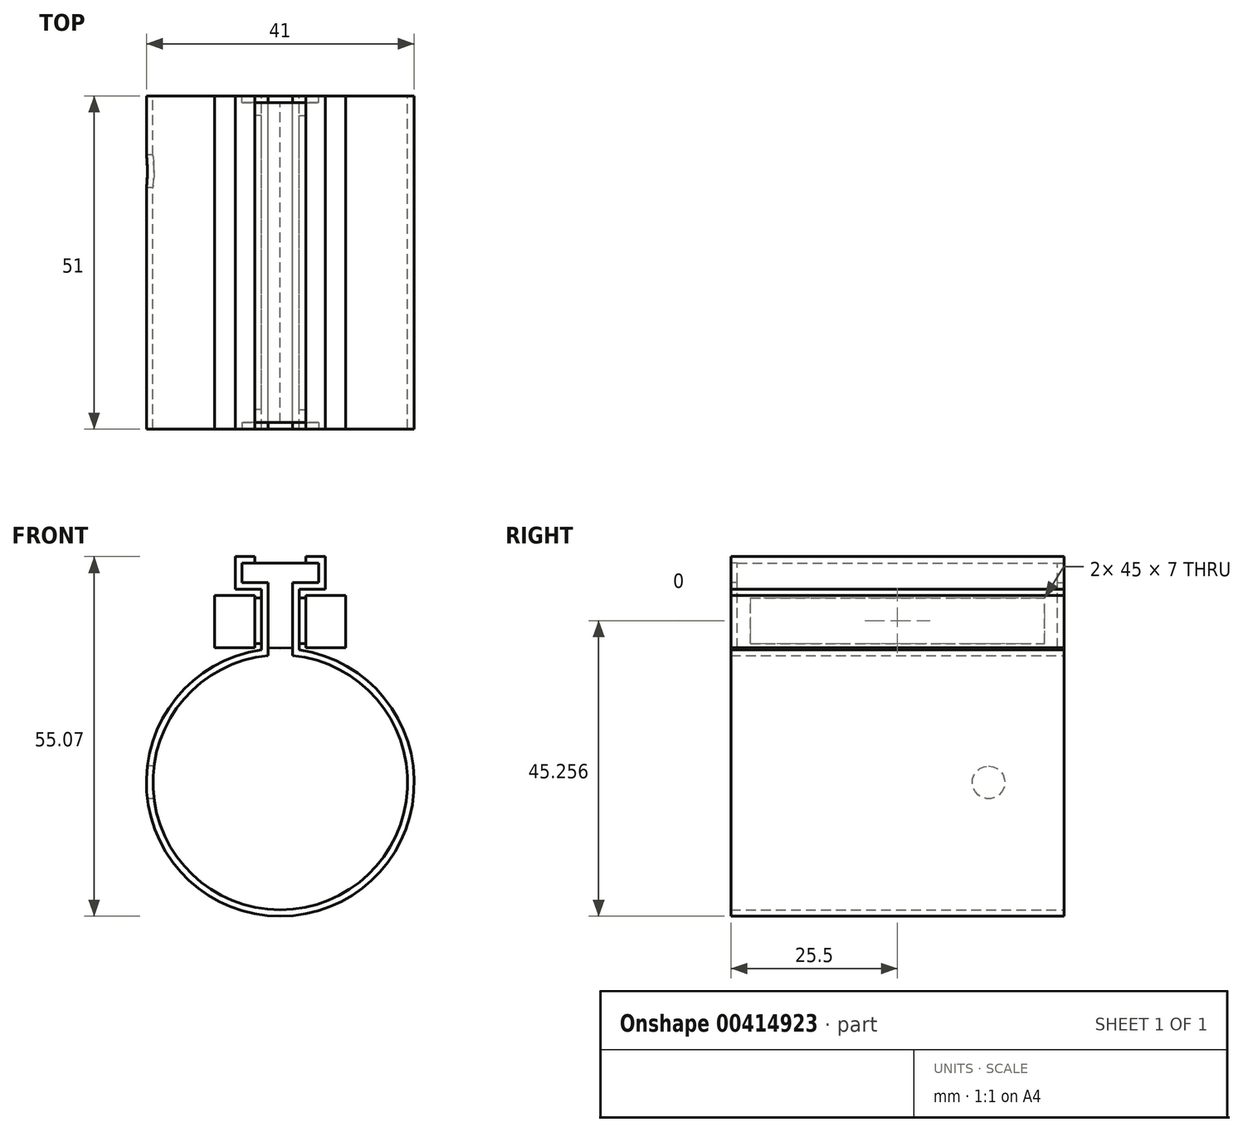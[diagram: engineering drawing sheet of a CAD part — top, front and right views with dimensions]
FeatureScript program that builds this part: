
annotation { "Feature Type Name" : "Feature", "Feature Type Description" : "" }
export const myFeature = defineFeature(function(context is Context, id is Id, definition is map)
    precondition{}
    {
        {
            var Q0;
            Q0=qCreatedBy(makeId("Front.planeOp"),FACE);
            var sketch = newSketch(context, id + "F0", { "sketchPlane" : qUnion([Q0])});
            skArc(sketch, "E0", {"start": v(0, -19.5) * mm, "mid": v(19.48, -0.94) * mm, "end": v(1.88, 19.4) * mm});
            skLineSegment(sketch, "E1", {"start": v(0, 19.5) * mm, "end": v(0, 19.5) * mm});
            skLineSegment(sketch, "E2", {"start": v(1.88, 30.57) * mm, "end": v(5.88, 30.57) * mm});
            skLineSegment(sketch, "E3", {"start": v(5.88, 30.57) * mm, "end": v(5.88, 33.57) * mm});
            skLineSegment(sketch, "E4", {"start": v(5.88, 33.57) * mm, "end": v(3.88, 33.57) * mm});
            skLineSegment(sketch, "E5.0", {"start": v(6.88, 34.57) * mm, "end": v(3.88, 34.57) * mm});
            skLineSegment(sketch, "E5.1", {"start": v(6.88, 29.57) * mm, "end": v(6.88, 34.57) * mm});
            skLineSegment(sketch, "E5.2", {"start": v(2.88, 29.57) * mm, "end": v(6.88, 29.57) * mm});
            skLineSegment(sketch, "E5.3", {"start": v(2.88, 20.3) * mm, "end": v(2.88, 29.57) * mm});
            skLineSegment(sketch, "E6", {"start": v(3.88, 34.57) * mm, "end": v(3.88, 33.57) * mm});
            skLineSegment(sketch, "E7.trimOffspring", {"start": v(1.88, 20.58) * mm, "end": v(1.88, 30.57) * mm});
            skArc(sketch, "E8", {"start": v(0, -20.5) * mm, "mid": v(20.45, -1.44) * mm, "end": v(2.88, 20.3) * mm});
            skLineSegment(sketch, "E9", {"start": v(0, -19.5) * mm, "end": v(0, -20.5) * mm});
            skLineSegment(sketch, "E10", {"start": v(1.88, 20.58) * mm, "end": v(1.88, 19.4) * mm});
            skLineSegment(sketch, "E11", {"start": v(2.88, 21.26) * mm, "end": v(3.88, 21.26) * mm});
            skLineSegment(sketch, "E12", {"start": v(3.88, 21.26) * mm, "end": v(3.88, 28.26) * mm});
            skLineSegment(sketch, "E13", {"start": v(3.88, 28.26) * mm, "end": v(2.88, 28.26) * mm});
            skLineSegment(sketch, "E14", {"start": v(3.88, 28.26) * mm, "end": v(3.88, 28.64) * mm});
            skLineSegment(sketch, "E15", {"start": v(3.88, 28.64) * mm, "end": v(10.04, 28.64) * mm});
            skLineSegment(sketch, "E16", {"start": v(10.04, 28.64) * mm, "end": v(10.04, 20.64) * mm});
            skLineSegment(sketch, "E17", {"start": v(3.88, 21.26) * mm, "end": v(3.88, 20.64) * mm});
            skLineSegment(sketch, "E18", {"start": v(3.88, 20.64) * mm, "end": v(10.04, 20.64) * mm});
            skLineSegment(sketch, "E19", {"start": v(0, 20.56) * mm, "end": v(0, 33.57) * mm});
            skLineSegment(sketch, "E20", {"start": v(0, 33.57) * mm, "end": v(3.88, 33.57) * mm});
            skLineSegment(sketch, "E21", {"start": v(3.88, 33.57) * mm, "end": v(3.88, 33.57) * mm});
            skLineSegment(sketch, "E22", {"start": v(5.88, 33.57) * mm, "end": v(5.88, 30.57) * mm});
            skLineSegment(sketch, "E23", {"start": v(1.88, 30.57) * mm, "end": v(1.88, 20.58) * mm});
            skLineSegment(sketch, "E24", {"start": v(0, 20.56) * mm, "end": v(1.88, 20.58) * mm});
            skSolve(sketch);
        }
        {
            var Q0;
            Q0 = qSketchRegion(id + "F0", true);
            extrude(context, id + "F1", {"entities" : qUnion([Q0]), "endBound" : BoundingType.SYMMETRIC, "depth" : 51 * mm});
        }
        {
            var Q0;
            Q0=makeQuery(id+"F1.opExtrude","CAP_FACE",FACE,{"disambiguationData":[OSD([sQuery(id+"F0.wireOp",EDGE,"E0"),sQuery(id+"F0.wireOp",EDGE,"E2"),sQuery(id+"F0.wireOp",EDGE,"E3"),sQuery(id+"F0.wireOp",EDGE,"E4"),sQuery(id+"F0.wireOp",EDGE,"E5.0"),sQuery(id+"F0.wireOp",EDGE,"E5.1"),sQuery(id+"F0.wireOp",EDGE,"E5.2"),sQuery(id+"F0.wireOp",EDGE,"E5.3"),sQuery(id+"F0.wireOp",EDGE,"E6"),sQuery(id+"F0.wireOp",EDGE,"E7.trimOffspring"),sQuery(id+"F0.wireOp",EDGE,"E8"),sQuery(id+"F0.wireOp",EDGE,"E9"),sQuery(id+"F0.wireOp",EDGE,"E10"),sQuery(id+"F0.wireOp",EDGE,"E11"),sQuery(id+"F0.wireOp",EDGE,"E13"),sQuery(id+"F0.wireOp",EDGE,"E14"),sQuery(id+"F0.wireOp",EDGE,"E15"),sQuery(id+"F0.wireOp",EDGE,"E16"),sQuery(id+"F0.wireOp",EDGE,"E17"),sQuery(id+"F0.wireOp",EDGE,"E18")])],"isStart":false});
            var sketch = newSketch(context, id + "F2", { "sketchPlane" : qUnion([Q0])});
            skArc(sketch, "E25.0", {"start": v(0, -19.5) * mm, "mid": v(19.48, -0.94) * mm, "end": v(1.88, 19.4) * mm});
            skPoint(sketch, "E25.1", {"position": v(0, 19.5) * mm});
            skLineSegment(sketch, "E25.2", {"start": v(1.88, 30.57) * mm, "end": v(5.88, 30.57) * mm});
            skLineSegment(sketch, "E25.3", {"start": v(5.88, 30.57) * mm, "end": v(5.88, 33.57) * mm});
            skLineSegment(sketch, "E25.4", {"start": v(5.88, 33.57) * mm, "end": v(3.88, 33.57) * mm});
            skLineSegment(sketch, "E25.5", {"start": v(6.88, 34.57) * mm, "end": v(3.88, 34.57) * mm});
            skLineSegment(sketch, "E25.6", {"start": v(6.88, 29.57) * mm, "end": v(6.88, 34.57) * mm});
            skLineSegment(sketch, "E25.7", {"start": v(2.88, 29.57) * mm, "end": v(6.88, 29.57) * mm});
            skLineSegment(sketch, "E25.8", {"start": v(2.88, 20.3) * mm, "end": v(2.88, 29.57) * mm});
            skLineSegment(sketch, "E25.9", {"start": v(3.88, 34.57) * mm, "end": v(3.88, 33.57) * mm});
            skLineSegment(sketch, "E25.10", {"start": v(1.88, 20.58) * mm, "end": v(1.88, 30.57) * mm});
            skArc(sketch, "E25.11", {"start": v(0, -20.5) * mm, "mid": v(20.45, -1.44) * mm, "end": v(2.88, 20.3) * mm});
            skLineSegment(sketch, "E25.12", {"start": v(0, -19.5) * mm, "end": v(0, -20.5) * mm});
            skLineSegment(sketch, "E25.13", {"start": v(1.88, 20.58) * mm, "end": v(1.88, 19.4) * mm});
            skLineSegment(sketch, "E25.14", {"start": v(2.88, 21.26) * mm, "end": v(3.88, 21.26) * mm});
            skLineSegment(sketch, "E25.15", {"start": v(3.88, 21.26) * mm, "end": v(3.88, 28.26) * mm});
            skLineSegment(sketch, "E25.16", {"start": v(3.88, 28.26) * mm, "end": v(2.88, 28.26) * mm});
            skLineSegment(sketch, "E25.17", {"start": v(3.88, 28.26) * mm, "end": v(3.88, 28.64) * mm});
            skLineSegment(sketch, "E25.18", {"start": v(3.88, 28.64) * mm, "end": v(10.04, 28.64) * mm});
            skLineSegment(sketch, "E25.19", {"start": v(10.04, 28.64) * mm, "end": v(10.04, 20.64) * mm});
            skLineSegment(sketch, "E25.20", {"start": v(3.88, 21.26) * mm, "end": v(3.88, 20.64) * mm});
            skLineSegment(sketch, "E25.21", {"start": v(3.88, 20.64) * mm, "end": v(10.04, 20.64) * mm});
            skLineSegment(sketch, "E25.22", {"start": v(10.04, 28.64) * mm, "end": v(10.04, 20.64) * mm});
            skSolve(sketch);
        }
        {
            var Q0;
            {var subQ0=sQuery(id+"F2.wireOp",EDGE,"E25.14");Q0=makeQuery(id+"F2.imprint","IMPRINT",FACE,{"disambiguationData":[TD([[makeQuery(id+"F2.imprint","IMPRINT",EDGE,{"derivedFrom":subQ0}),1.0]])]});}
            extrude(context, id + "F3", {"entities" : qUnion([Q0]), "operationType" : NewBodyOperationType.REMOVE, "oppositeDirection" : true, "depth" : 3 * mm});
        }
        {
            var Q0;
            Q0=makeQuery(id+"F1.opExtrude","CAP_FACE",FACE,{"disambiguationData":[OSD([sQuery(id+"F0.wireOp",EDGE,"E0"),sQuery(id+"F0.wireOp",EDGE,"E2"),sQuery(id+"F0.wireOp",EDGE,"E3"),sQuery(id+"F0.wireOp",EDGE,"E4"),sQuery(id+"F0.wireOp",EDGE,"E5.0"),sQuery(id+"F0.wireOp",EDGE,"E5.1"),sQuery(id+"F0.wireOp",EDGE,"E5.2"),sQuery(id+"F0.wireOp",EDGE,"E5.3"),sQuery(id+"F0.wireOp",EDGE,"E6"),sQuery(id+"F0.wireOp",EDGE,"E7.trimOffspring"),sQuery(id+"F0.wireOp",EDGE,"E8"),sQuery(id+"F0.wireOp",EDGE,"E9"),sQuery(id+"F0.wireOp",EDGE,"E10"),sQuery(id+"F0.wireOp",EDGE,"E11"),sQuery(id+"F0.wireOp",EDGE,"E13"),sQuery(id+"F0.wireOp",EDGE,"E14"),sQuery(id+"F0.wireOp",EDGE,"E15"),sQuery(id+"F0.wireOp",EDGE,"E16"),sQuery(id+"F0.wireOp",EDGE,"E17"),sQuery(id+"F0.wireOp",EDGE,"E18")])],"isStart":true});
            var sketch = newSketch(context, id + "F4", { "sketchPlane" : qUnion([Q0])});
            skArc(sketch, "E26.0", {"start": v(0, -19.5) * mm, "mid": v(-19.48, -0.94) * mm, "end": v(-1.88, 19.4) * mm});
            skPoint(sketch, "E26.1", {"position": v(0, 19.5) * mm});
            skLineSegment(sketch, "E26.2", {"start": v(-1.88, 30.57) * mm, "end": v(-5.88, 30.57) * mm});
            skLineSegment(sketch, "E26.3", {"start": v(-5.88, 30.57) * mm, "end": v(-5.88, 33.57) * mm});
            skLineSegment(sketch, "E26.4", {"start": v(-5.88, 33.57) * mm, "end": v(-3.88, 33.57) * mm});
            skLineSegment(sketch, "E26.5", {"start": v(-6.88, 34.57) * mm, "end": v(-3.88, 34.57) * mm});
            skLineSegment(sketch, "E26.6", {"start": v(-6.88, 29.57) * mm, "end": v(-6.88, 34.57) * mm});
            skLineSegment(sketch, "E26.7", {"start": v(-2.88, 29.57) * mm, "end": v(-6.88, 29.57) * mm});
            skLineSegment(sketch, "E26.8", {"start": v(-2.88, 20.3) * mm, "end": v(-2.88, 29.57) * mm});
            skLineSegment(sketch, "E26.9", {"start": v(-3.88, 34.57) * mm, "end": v(-3.88, 33.57) * mm});
            skLineSegment(sketch, "E26.10", {"start": v(-1.88, 20.58) * mm, "end": v(-1.88, 30.57) * mm});
            skArc(sketch, "E26.11", {"start": v(0, -20.5) * mm, "mid": v(-20.45, -1.44) * mm, "end": v(-2.88, 20.3) * mm});
            skLineSegment(sketch, "E26.12", {"start": v(0, -19.5) * mm, "end": v(0, -20.5) * mm});
            skLineSegment(sketch, "E26.13", {"start": v(-1.88, 20.58) * mm, "end": v(-1.88, 19.4) * mm});
            skLineSegment(sketch, "E26.14", {"start": v(-2.88, 21.26) * mm, "end": v(-3.88, 21.26) * mm});
            skLineSegment(sketch, "E26.15", {"start": v(-3.88, 21.26) * mm, "end": v(-3.88, 28.26) * mm});
            skLineSegment(sketch, "E26.16", {"start": v(-3.88, 28.26) * mm, "end": v(-2.88, 28.26) * mm});
            skLineSegment(sketch, "E26.17", {"start": v(-3.88, 28.26) * mm, "end": v(-3.88, 28.64) * mm});
            skLineSegment(sketch, "E26.18", {"start": v(-3.88, 28.64) * mm, "end": v(-10.04, 28.64) * mm});
            skLineSegment(sketch, "E26.19", {"start": v(-10.04, 28.64) * mm, "end": v(-10.04, 20.64) * mm});
            skLineSegment(sketch, "E26.20", {"start": v(-3.88, 21.26) * mm, "end": v(-3.88, 20.64) * mm});
            skLineSegment(sketch, "E26.21", {"start": v(-3.88, 20.64) * mm, "end": v(-10.04, 20.64) * mm});
            skLineSegment(sketch, "E26.22.0", {"start": v(-10.04, 20.64) * mm, "end": v(-10.04, 28.64) * mm});
            skLineSegment(sketch, "E26.22.2", {"start": v(-10.04, 28.64) * mm, "end": v(-10.04, 20.64) * mm});
            skSolve(sketch);
        }
        {
            var Q0;
            {var subQ0=sQuery(id+"F4.wireOp",EDGE,"E26.14");Q0=makeQuery(id+"F4.imprint","IMPRINT",FACE,{"disambiguationData":[TD([[makeQuery(id+"F4.imprint","IMPRINT",EDGE,{"derivedFrom":subQ0}),-1.0]])]});}
            extrude(context, id + "F5", {"entities" : qUnion([Q0]), "operationType" : NewBodyOperationType.REMOVE, "oppositeDirection" : true, "depth" : 3 * mm});
        }
        {
            var Q0;
            {var subQ0=sQuery(id+"F0.wireOp",EDGE,"E10");var subQ1=sQuery(id+"F0.wireOp",EDGE,"E9");var subQ2=sQuery(id+"F0.wireOp",EDGE,"E8");var subQ3=sQuery(id+"F0.wireOp",EDGE,"E19");var subQ4=sQuery(id+"F0.wireOp",EDGE,"E5.3");var subQ5=sQuery(id+"F0.wireOp",EDGE,"E5.2");var subQ6=sQuery(id+"F0.wireOp",EDGE,"E13");var subQ7=sQuery(id+"F0.wireOp",EDGE,"E11");var subQ8=sQuery(id+"F0.wireOp",EDGE,"E0");var subQ9=sQuery(id+"F0.wireOp",EDGE,"E5.0");var subQ10=sQuery(id+"F0.wireOp",EDGE,"E5.1");var subQ11=sQuery(id+"F0.wireOp",EDGE,"E20");var subQ12=sQuery(id+"F0.wireOp",EDGE,"E21");var subQ13=sQuery(id+"F0.wireOp",EDGE,"E24");var subQ14=makeQuery(id+"F3.boolean.opBoolean","SPLIT",FACE,{"disambiguationData":[TD([makeQuery(id+"F1.opExtrude","SWEPT_FACE",FACE,{"disambiguationData":[OSD([subQ8])]})])],"derivedFrom":makeQuery(id+"F1.opExtrude","CAP_FACE",FACE,{"disambiguationData":[OSD([subQ8,subQ9,subQ10,subQ5,subQ4,subQ2,subQ1,subQ0,subQ7,subQ6,sQuery(id+"F0.wireOp",EDGE,"E14"),sQuery(id+"F0.wireOp",EDGE,"E15"),sQuery(id+"F0.wireOp",EDGE,"E16"),sQuery(id+"F0.wireOp",EDGE,"E17"),sQuery(id+"F0.wireOp",EDGE,"E18"),subQ3,subQ11,subQ12,subQ13])],"isStart":false})});Q0=makeQuery(id+"F10.boolean.opBoolean","MERGE",FACE,{"derivedFrom":[subQ14,makeQuery(id+"F10.opPattern","COPY",FACE,{"derivedFrom":subQ14,"instanceName":"1"})]});}
            var sketch = newSketch(context, id + "F6", { "sketchPlane" : qUnion([Q0])});
            skArc(sketch, "E27.0", {"start": v(0, -19.5) * mm, "mid": v(19.48, -0.94) * mm, "end": v(1.88, 19.4) * mm});
            skPoint(sketch, "E27.1", {"position": v(0, 19.5) * mm});
            skLineSegment(sketch, "E27.2", {"start": v(1.88, 30.57) * mm, "end": v(5.88, 30.57) * mm});
            skLineSegment(sketch, "E27.3", {"start": v(5.88, 30.57) * mm, "end": v(5.88, 33.57) * mm});
            skLineSegment(sketch, "E27.4", {"start": v(5.88, 33.57) * mm, "end": v(3.88, 33.57) * mm});
            skLineSegment(sketch, "E27.5", {"start": v(6.88, 34.57) * mm, "end": v(3.88, 34.57) * mm});
            skLineSegment(sketch, "E27.6", {"start": v(6.88, 29.57) * mm, "end": v(6.88, 34.57) * mm});
            skLineSegment(sketch, "E27.7", {"start": v(2.88, 29.57) * mm, "end": v(6.88, 29.57) * mm});
            skLineSegment(sketch, "E27.8", {"start": v(2.88, 20.3) * mm, "end": v(2.88, 29.57) * mm});
            skLineSegment(sketch, "E27.9", {"start": v(3.88, 34.57) * mm, "end": v(3.88, 33.57) * mm});
            skLineSegment(sketch, "E27.10", {"start": v(1.88, 20.58) * mm, "end": v(1.88, 30.57) * mm});
            skArc(sketch, "E27.11", {"start": v(0, -20.5) * mm, "mid": v(20.45, -1.44) * mm, "end": v(2.88, 20.3) * mm});
            skLineSegment(sketch, "E27.12", {"start": v(0, -19.5) * mm, "end": v(0, -20.5) * mm});
            skLineSegment(sketch, "E27.13", {"start": v(1.88, 20.58) * mm, "end": v(1.88, 19.4) * mm});
            skLineSegment(sketch, "E27.14", {"start": v(2.88, 21.26) * mm, "end": v(3.88, 21.26) * mm});
            skLineSegment(sketch, "E27.15", {"start": v(3.88, 21.26) * mm, "end": v(3.88, 28.26) * mm});
            skLineSegment(sketch, "E27.16", {"start": v(3.88, 28.26) * mm, "end": v(2.88, 28.26) * mm});
            skLineSegment(sketch, "E27.17", {"start": v(3.88, 28.26) * mm, "end": v(3.88, 28.64) * mm});
            skLineSegment(sketch, "E27.18", {"start": v(3.88, 28.64) * mm, "end": v(10.04, 28.64) * mm});
            skLineSegment(sketch, "E27.19", {"start": v(10.04, 28.64) * mm, "end": v(10.04, 20.64) * mm});
            skLineSegment(sketch, "E27.20", {"start": v(3.88, 21.26) * mm, "end": v(3.88, 20.64) * mm});
            skLineSegment(sketch, "E27.21", {"start": v(3.88, 20.64) * mm, "end": v(10.04, 20.64) * mm});
            skLineSegment(sketch, "E27.22", {"start": v(0, 20.56) * mm, "end": v(0, 33.57) * mm});
            skLineSegment(sketch, "E27.23", {"start": v(0, 33.57) * mm, "end": v(3.88, 33.57) * mm});
            skLineSegment(sketch, "E27.24", {"start": v(3.88, 33.57) * mm, "end": v(3.88, 33.57) * mm});
            skLineSegment(sketch, "E27.25", {"start": v(5.88, 33.57) * mm, "end": v(5.88, 30.57) * mm});
            skLineSegment(sketch, "E27.26", {"start": v(1.88, 30.57) * mm, "end": v(1.88, 20.58) * mm});
            skLineSegment(sketch, "E27.27", {"start": v(0, 20.56) * mm, "end": v(1.88, 20.58) * mm});
            skLineSegment(sketch, "E27.28.0", {"start": v(6.88, 29.57) * mm, "end": v(6.88, 34.57) * mm});
            skLineSegment(sketch, "E27.28.2", {"start": v(6.88, 34.57) * mm, "end": v(6.88, 29.57) * mm});
            skSolve(sketch);
        }
        {
            var Q0;
            Q0=makeQuery(id+"F6.imprint","IMPRINT",FACE,{"disambiguationData":[TD([[makeQuery(id+"F6.imprint","IMPRINT",EDGE,{"derivedFrom":sQuery(id+"F6.wireOp",EDGE,"E27.2")}),1.0]])]});
            extrude(context, id + "F7", {"entities" : qUnion([Q0]), "operationType" : NewBodyOperationType.REMOVE, "oppositeDirection" : true, "depth" : 1 * mm});
        }
        {
            var Q0;
            {var subQ0=sQuery(id+"F0.wireOp",EDGE,"E10");var subQ1=sQuery(id+"F0.wireOp",EDGE,"E9");var subQ2=sQuery(id+"F0.wireOp",EDGE,"E8");var subQ3=sQuery(id+"F0.wireOp",EDGE,"E19");var subQ4=sQuery(id+"F0.wireOp",EDGE,"E5.3");var subQ5=sQuery(id+"F0.wireOp",EDGE,"E5.2");var subQ6=sQuery(id+"F0.wireOp",EDGE,"E13");var subQ7=sQuery(id+"F0.wireOp",EDGE,"E11");var subQ8=sQuery(id+"F0.wireOp",EDGE,"E0");var subQ9=sQuery(id+"F0.wireOp",EDGE,"E5.0");var subQ10=sQuery(id+"F0.wireOp",EDGE,"E5.1");var subQ11=sQuery(id+"F0.wireOp",EDGE,"E20");var subQ12=sQuery(id+"F0.wireOp",EDGE,"E21");var subQ13=sQuery(id+"F0.wireOp",EDGE,"E24");var subQ14=makeQuery(id+"F5.boolean.opBoolean","SPLIT",FACE,{"disambiguationData":[TD([makeQuery(id+"F1.opExtrude","SWEPT_FACE",FACE,{"disambiguationData":[OSD([subQ8])]})])],"derivedFrom":makeQuery(id+"F1.opExtrude","CAP_FACE",FACE,{"disambiguationData":[OSD([subQ8,subQ9,subQ10,subQ5,subQ4,subQ2,subQ1,subQ0,subQ7,subQ6,sQuery(id+"F0.wireOp",EDGE,"E14"),sQuery(id+"F0.wireOp",EDGE,"E15"),sQuery(id+"F0.wireOp",EDGE,"E16"),sQuery(id+"F0.wireOp",EDGE,"E17"),sQuery(id+"F0.wireOp",EDGE,"E18"),subQ3,subQ11,subQ12,subQ13])],"isStart":true})});Q0=makeQuery(id+"F10.boolean.opBoolean","MERGE",FACE,{"derivedFrom":[subQ14,makeQuery(id+"F10.opPattern","COPY",FACE,{"derivedFrom":subQ14,"instanceName":"1"})]});}
            var sketch = newSketch(context, id + "F8", { "sketchPlane" : qUnion([Q0])});
            skArc(sketch, "E28.0", {"start": v(0, -19.5) * mm, "mid": v(-19.48, -0.94) * mm, "end": v(-1.88, 19.4) * mm});
            skPoint(sketch, "E28.1", {"position": v(0, 19.5) * mm});
            skLineSegment(sketch, "E28.2", {"start": v(-1.88, 30.57) * mm, "end": v(-5.88, 30.57) * mm});
            skLineSegment(sketch, "E28.3", {"start": v(-5.88, 30.57) * mm, "end": v(-5.88, 33.57) * mm});
            skLineSegment(sketch, "E28.4", {"start": v(-5.88, 33.57) * mm, "end": v(-3.88, 33.57) * mm});
            skLineSegment(sketch, "E28.5", {"start": v(-6.88, 34.57) * mm, "end": v(-3.88, 34.57) * mm});
            skLineSegment(sketch, "E28.6", {"start": v(-6.88, 29.57) * mm, "end": v(-6.88, 34.57) * mm});
            skLineSegment(sketch, "E28.7", {"start": v(-2.88, 29.57) * mm, "end": v(-6.88, 29.57) * mm});
            skLineSegment(sketch, "E28.8", {"start": v(-2.88, 20.3) * mm, "end": v(-2.88, 29.57) * mm});
            skLineSegment(sketch, "E28.9", {"start": v(-3.88, 34.57) * mm, "end": v(-3.88, 33.57) * mm});
            skLineSegment(sketch, "E28.10", {"start": v(-1.88, 20.58) * mm, "end": v(-1.88, 30.57) * mm});
            skArc(sketch, "E28.11", {"start": v(0, -20.5) * mm, "mid": v(-20.45, -1.44) * mm, "end": v(-2.88, 20.3) * mm});
            skLineSegment(sketch, "E28.12", {"start": v(0, -19.5) * mm, "end": v(0, -20.5) * mm});
            skLineSegment(sketch, "E28.13", {"start": v(-1.88, 20.58) * mm, "end": v(-1.88, 19.4) * mm});
            skLineSegment(sketch, "E28.14", {"start": v(-2.88, 21.26) * mm, "end": v(-3.88, 21.26) * mm});
            skLineSegment(sketch, "E28.15", {"start": v(-3.88, 21.26) * mm, "end": v(-3.88, 28.26) * mm});
            skLineSegment(sketch, "E28.16", {"start": v(-3.88, 28.26) * mm, "end": v(-2.88, 28.26) * mm});
            skLineSegment(sketch, "E28.17", {"start": v(-3.88, 28.26) * mm, "end": v(-3.88, 28.64) * mm});
            skLineSegment(sketch, "E28.18", {"start": v(-3.88, 28.64) * mm, "end": v(-10.04, 28.64) * mm});
            skLineSegment(sketch, "E28.19", {"start": v(-10.04, 28.64) * mm, "end": v(-10.04, 20.64) * mm});
            skLineSegment(sketch, "E28.20", {"start": v(-3.88, 21.26) * mm, "end": v(-3.88, 20.64) * mm});
            skLineSegment(sketch, "E28.21", {"start": v(-3.88, 20.64) * mm, "end": v(-10.04, 20.64) * mm});
            skLineSegment(sketch, "E28.22", {"start": v(0, 20.56) * mm, "end": v(0, 33.57) * mm});
            skLineSegment(sketch, "E28.23", {"start": v(0, 33.57) * mm, "end": v(-3.88, 33.57) * mm});
            skLineSegment(sketch, "E28.24", {"start": v(-3.88, 33.57) * mm, "end": v(-3.88, 33.57) * mm});
            skLineSegment(sketch, "E28.25", {"start": v(-5.88, 33.57) * mm, "end": v(-5.88, 30.57) * mm});
            skLineSegment(sketch, "E28.26", {"start": v(-1.88, 30.57) * mm, "end": v(-1.88, 20.58) * mm});
            skLineSegment(sketch, "E28.27", {"start": v(0, 20.56) * mm, "end": v(-1.88, 20.58) * mm});
            skSolve(sketch);
        }
        {
            var Q0;
            Q0=makeQuery(id+"F8.imprint","IMPRINT",FACE,{"disambiguationData":[TD([[makeQuery(id+"F8.imprint","IMPRINT",EDGE,{"derivedFrom":sQuery(id+"F8.wireOp",EDGE,"E28.2")}),-1.0]])]});
            extrude(context, id + "F9", {"entities" : qUnion([Q0]), "operationType" : NewBodyOperationType.REMOVE, "oppositeDirection" : true, "depth" : 1 * mm});
        }
        {
            var Q0;
            Q0=makeQuery(id+"F1.opExtrude","SWEPT_BODY",BODY,{"disambiguationData":[OSD([sQuery(id+"F0.wireOp",EDGE,"E0"),sQuery(id+"F0.wireOp",EDGE,"E2"),sQuery(id+"F0.wireOp",EDGE,"E3"),sQuery(id+"F0.wireOp",EDGE,"E4"),sQuery(id+"F0.wireOp",EDGE,"E5.0"),sQuery(id+"F0.wireOp",EDGE,"E5.1"),sQuery(id+"F0.wireOp",EDGE,"E5.2"),sQuery(id+"F0.wireOp",EDGE,"E5.3"),sQuery(id+"F0.wireOp",EDGE,"E6"),sQuery(id+"F0.wireOp",EDGE,"E7.trimOffspring"),sQuery(id+"F0.wireOp",EDGE,"E8"),sQuery(id+"F0.wireOp",EDGE,"E9"),sQuery(id+"F0.wireOp",EDGE,"E10"),sQuery(id+"F0.wireOp",EDGE,"E11"),sQuery(id+"F0.wireOp",EDGE,"E13"),sQuery(id+"F0.wireOp",EDGE,"E14"),sQuery(id+"F0.wireOp",EDGE,"E15"),sQuery(id+"F0.wireOp",EDGE,"E16"),sQuery(id+"F0.wireOp",EDGE,"E17"),sQuery(id+"F0.wireOp",EDGE,"E18")])]});
            var Q1;
            Q1=qCreatedBy(makeId("Right.planeOp"),FACE);
            mirror(context, id + "F10", {"operationType" : NewBodyOperationType.ADD, "entities" : qUnion([Q0]), "mirrorPlane" : qUnion([Q1])});
        }
        {
            var Q0;
            Q0=qCreatedBy(makeId("Right.planeOp"),FACE);
            cPlane(context, id + "F11", {"entities" : qUnion([Q0]), "cplaneType" : CPlaneType.OFFSET, "offset" : 20.5 * mm, "oppositeDirection" : true, "width" : 150 * mm, "height" : 150 * mm});
        }
        {
            var Q0;
            Q0=qCreatedBy(id+"F11.planeOp",FACE);
            var sketch = newSketch(context, id + "F12", { "sketchPlane" : qUnion([Q0])});
            skLineSegment(sketch, "E29", {"start": v(22.95, 0) * mm, "end": v(13.95, 0) * mm});
            skSolve(sketch);
        }
        {
            var Q0;
            Q0=sQuery(id+"F12.wireOp",VERTEX,"E29.end");
            var Q1;
            Q1=makeQuery(id+"F1.opExtrude","SWEPT_BODY",BODY,{"disambiguationData":[OSD([sQuery(id+"F0.wireOp",EDGE,"E0"),sQuery(id+"F0.wireOp",EDGE,"E5.0"),sQuery(id+"F0.wireOp",EDGE,"E5.1"),sQuery(id+"F0.wireOp",EDGE,"E5.2"),sQuery(id+"F0.wireOp",EDGE,"E5.3"),sQuery(id+"F0.wireOp",EDGE,"E6"),sQuery(id+"F0.wireOp",EDGE,"E8"),sQuery(id+"F0.wireOp",EDGE,"E9"),sQuery(id+"F0.wireOp",EDGE,"E10"),sQuery(id+"F0.wireOp",EDGE,"E11"),sQuery(id+"F0.wireOp",EDGE,"E13"),sQuery(id+"F0.wireOp",EDGE,"E14"),sQuery(id+"F0.wireOp",EDGE,"E15"),sQuery(id+"F0.wireOp",EDGE,"E16"),sQuery(id+"F0.wireOp",EDGE,"E17"),sQuery(id+"F0.wireOp",EDGE,"E18"),sQuery(id+"F0.wireOp",EDGE,"E19"),sQuery(id+"F0.wireOp",EDGE,"E20"),sQuery(id+"F0.wireOp",EDGE,"E24")])]});
            hole(context, id + "F13", {"style" : HoleStyle.SIMPLE, "endStyle" : HoleEndStyle.BLIND, "oppositeDirection" : true, "holeDiameter" : 5 * mm, "holeDepth" : 6 * mm, "isTappedThrough" : true, "tappedDepth" : 12 * mm, "tapClearance" : 3, "startFromSketch" : true, "locations" : qUnion([Q0]), "scope" : qUnion([Q1])});
        }
    });
